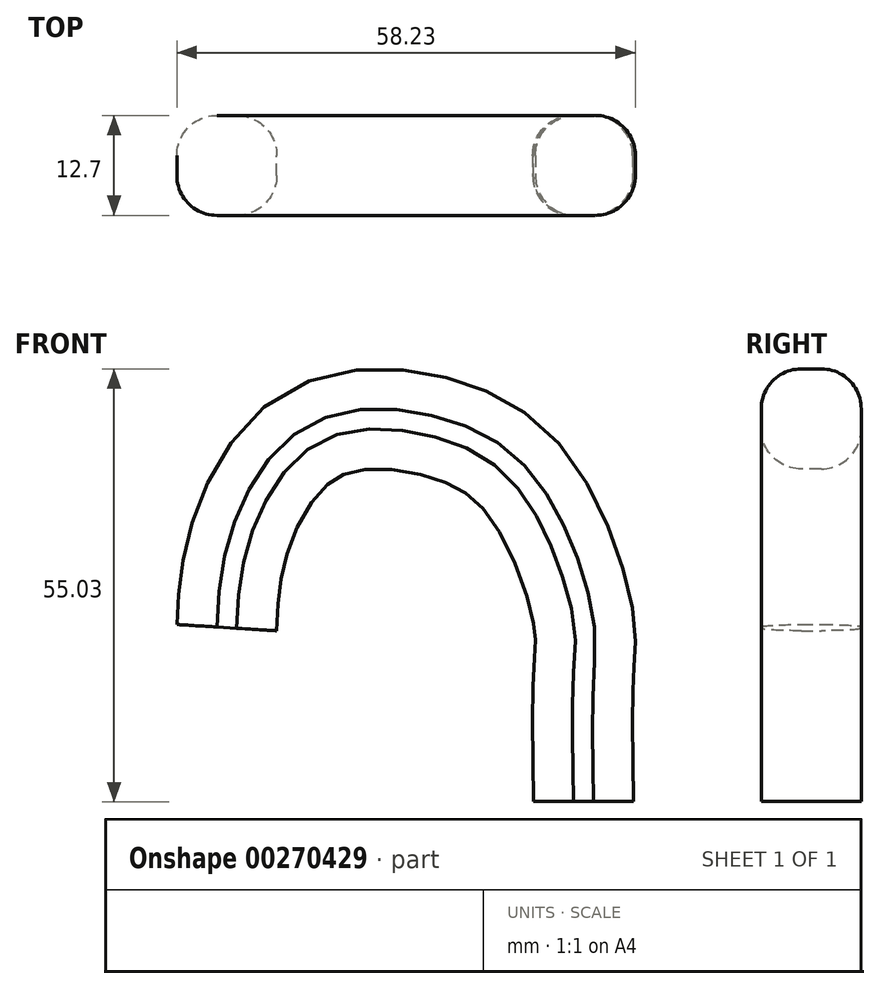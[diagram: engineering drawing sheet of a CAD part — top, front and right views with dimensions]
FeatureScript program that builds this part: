
annotation { "Feature Type Name" : "Feature", "Feature Type Description" : "" }
export const myFeature = defineFeature(function(context is Context, id is Id, definition is map)
    precondition{}
    {
        {
            var Q0;
            Q0=qCreatedBy(makeId("Front.planeOp"),FACE);
            var sketch = newSketch(context, id + "F0", { "sketchPlane" : qUnion([Q0])});
            skFitSpline(sketch, "E0", {"points": [v(0, 0) * mm, v(0, 16.36) * mm, v(0, 23.06) * mm, v(-6.9, 40) * mm, v(-19.12, 47.7) * mm, v(-34.68, 46.5) * mm, v(-43.75, 33.3) * mm, v(-45.33, 22.07) * mm], "startDerivative": vector(-2.11, 120.4) * mm, "endDerivative": vector(-3.76, -82.65) * mm});
            skSolve(sketch);
        }
        {
            var Q0;
            Q0=qCreatedBy(makeId("Top.planeOp"),FACE);
            var sketch = newSketch(context, id + "F1", { "sketchPlane" : qUnion([Q0])});
            skLineSegment(sketch, "E1.bottom", {"start": v(6.35, -6.35) * mm, "end": v(-6.35, -6.35) * mm});
            skLineSegment(sketch, "E1.top", {"start": v(6.35, 6.35) * mm, "end": v(-6.35, 6.35) * mm});
            skLineSegment(sketch, "E1.left", {"start": v(6.35, -6.35) * mm, "end": v(6.35, 6.35) * mm});
            skLineSegment(sketch, "E1.right", {"start": v(-6.35, -6.35) * mm, "end": v(-6.35, 6.35) * mm});
            skPoint(sketch, "E1.middle", {"position": v(0, 0) * mm});
            skSolve(sketch);
        }
        {
            var Q0;
            Q0=makeQuery(id+"F1.imprint","IMPRINT",FACE,{"disambiguationData":[TD([[makeQuery(id+"F1.imprint","IMPRINT",EDGE,{"derivedFrom":sQuery(id+"F1.wireOp",EDGE,"E1.bottom")}),-1.0]])]});
            var Q1;
            Q1=sQuery(id+"F0.wireOp",EDGE,"E0");
            sweep(context, id + "F2", {"profiles" : qUnion([Q0]), "path" : qUnion([Q1])});
        }
        {
            var Q0;
            Q0=makeQuery(id+"F2.opSweep","SWEPT_EDGE",EDGE,{"disambiguationData":[OSD([sQuery(id+"F0.wireOp",EDGE,"E0"),sQuery(id+"F1.wireOp",EDGE,"E1.bottom"),sQuery(id+"F1.wireOp",EDGE,"E1.left")])]});
            var Q1;
            Q1=makeQuery(id+"F2.opSweep","SWEPT_EDGE",EDGE,{"disambiguationData":[OSD([sQuery(id+"F0.wireOp",EDGE,"E0"),sQuery(id+"F1.wireOp",EDGE,"E1.top"),sQuery(id+"F1.wireOp",EDGE,"E1.left")])]});
            var Q2;
            Q2=makeQuery(id+"F2.opSweep","SWEPT_EDGE",EDGE,{"disambiguationData":[OSD([sQuery(id+"F0.wireOp",EDGE,"E0"),sQuery(id+"F1.wireOp",EDGE,"E1.bottom"),sQuery(id+"F1.wireOp",EDGE,"E1.right")])]});
            var Q3;
            Q3=makeQuery(id+"F2.opSweep","SWEPT_EDGE",EDGE,{"disambiguationData":[OSD([sQuery(id+"F0.wireOp",EDGE,"E0"),sQuery(id+"F1.wireOp",EDGE,"E1.top"),sQuery(id+"F1.wireOp",EDGE,"E1.right")])]});
            fillet(context, id + "F3", {"entities" : qUnion([Q0, Q1, Q2, Q3]), "radius" : 5.08 * mm, "tangentPropagation" : true, "allowEdgeOverflow" : false});
        }
    });
